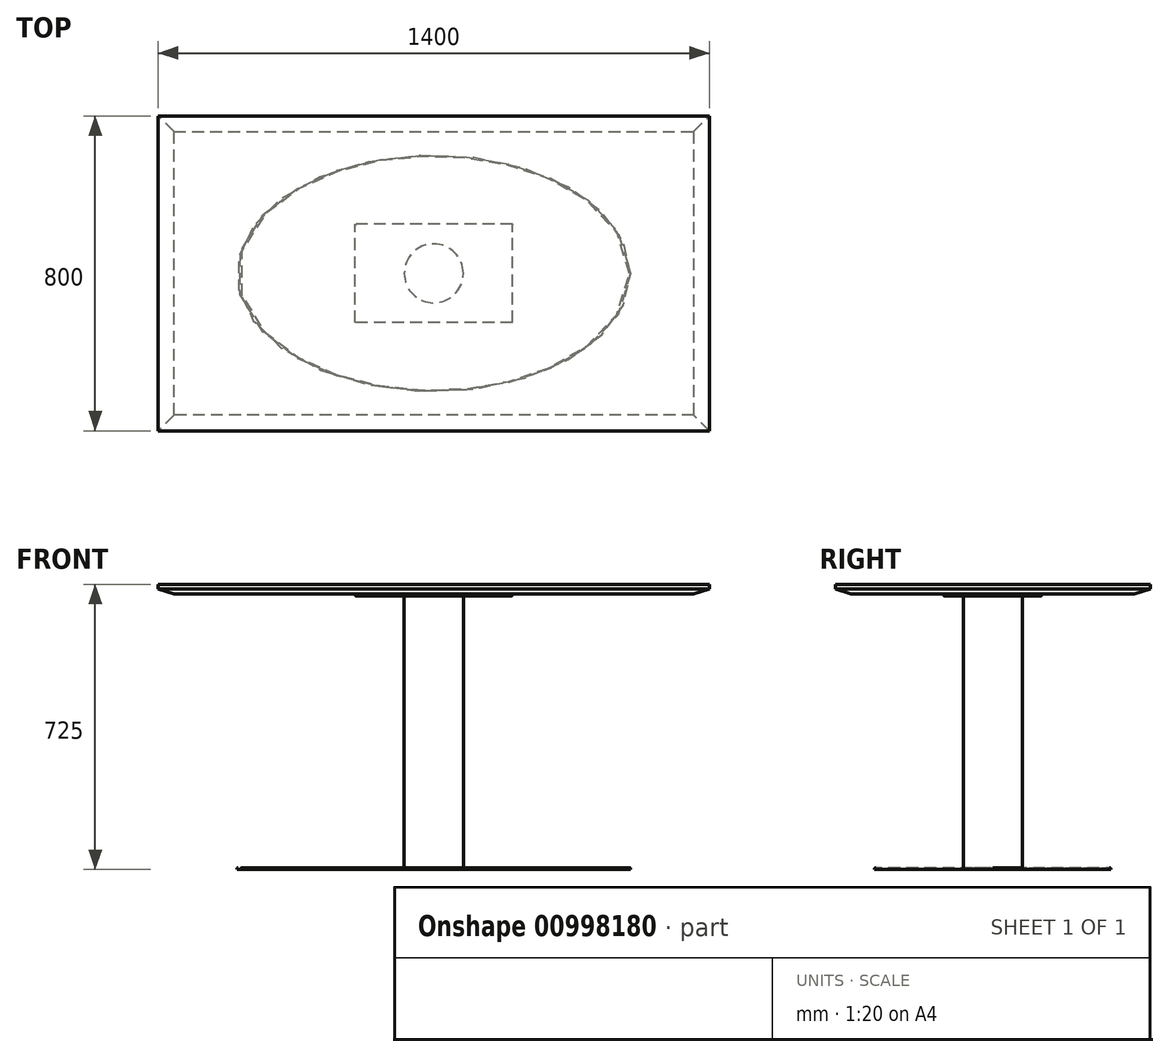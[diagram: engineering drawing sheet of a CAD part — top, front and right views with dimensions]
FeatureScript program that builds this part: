
annotation { "Feature Type Name" : "Feature", "Feature Type Description" : "" }
export const myFeature = defineFeature(function(context is Context, id is Id, definition is map)
    precondition{}
    {
        {
            var Q0;
            Q0=qCreatedBy(makeId("Top.planeOp"),FACE);
            var sketch = newSketch(context, id + "F0", { "sketchPlane" : qUnion([Q0])});
            skLineSegment(sketch, "E0.bottom", {"start": v(0, 0) * mm, "end": v(-1400, 0) * mm, "construction": true});
            skLineSegment(sketch, "E0.top", {"start": v(0, 800) * mm, "end": v(-1400, 800) * mm, "construction": true});
            skLineSegment(sketch, "E0.left", {"start": v(0, 0) * mm, "end": v(0, 800) * mm, "construction": true});
            skLineSegment(sketch, "E0.right", {"start": v(-1400, 0) * mm, "end": v(-1400, 800) * mm, "construction": true});
            skEllipse(sketch, "E1", {"center": v(-700, 400) * mm, "majorRadius": 500 * mm, "minorRadius": 300 * mm, "majorAxis": v(1, 0)});
            skPoint(sketch, "E1.centerSnap0", {"position": v(0, 400) * mm});
            skPoint(sketch, "E1.centerSnap1", {"position": v(-700, 0) * mm});
            skSolve(sketch);
        }
        {
            var Q0;
            Q0 = qSketchRegion(id + "F0", true);
            extrude(context, id + "F1", {"entities" : qUnion([Q0]), "depth" : 5 * mm, "offsetDistance" : 25 * mm});
        }
        {
            var Q0;
            Q0=makeQuery(id+"F1.opExtrude","CAP_FACE",FACE,{"disambiguationData":[OSD([sQuery(id+"F0.wireOp",EDGE,"E1")])],"isStart":false});
            fillet(context, id + "F2", {"entities" : qUnion([Q0]), "radius" : 3 * mm, "tangentPropagation" : true, "allowEdgeOverflow" : false});
        }
        {
            var Q0;
            Q0=makeQuery(id+"F1.opExtrude","CAP_FACE",FACE,{"disambiguationData":[OSD([sQuery(id+"F0.wireOp",EDGE,"E1")])],"isStart":false});
            cPlane(context, id + "F3", {"entities" : qUnion([Q0]), "cplaneType" : CPlaneType.OFFSET, "offset" : 0 * mm, "width" : 150 * mm, "height" : 150 * mm});
        }
        {
            var Q0;
            Q0=qCreatedBy(id+"F3.planeOp",FACE);
            var sketch = newSketch(context, id + "F4", { "sketchPlane" : qUnion([Q0])});
            skLineSegment(sketch, "E2", {"start": v(0, 0) * mm, "end": v(-700, 0) * mm, "construction": true});
            skLineSegment(sketch, "E3", {"start": v(-700, 0) * mm, "end": v(-700, 400) * mm, "construction": true});
            skCircle(sketch, "E4", {"center": v(-700, 400) * mm, "radius": 75 * mm});
            skSolve(sketch);
        }
        {
            var Q0;
            Q0 = qSketchRegion(id + "F4", true);
            extrude(context, id + "F5", {"entities" : qUnion([Q0]), "operationType" : NewBodyOperationType.ADD, "depth" : 690 * mm, "offsetDistance" : 25 * mm});
        }
        {
            var Q0;
            Q0=makeQuery(id+"F5.opExtrude","CAP_FACE",FACE,{"disambiguationData":[OSD([sQuery(id+"F4.wireOp",EDGE,"E4")])],"isStart":false});
            cPlane(context, id + "F6", {"entities" : qUnion([Q0]), "cplaneType" : CPlaneType.OFFSET, "offset" : 0 * mm, "width" : 150 * mm, "height" : 150 * mm});
        }
        {
            var Q0;
            Q0=qCreatedBy(id+"F6.planeOp",FACE);
            var sketch = newSketch(context, id + "F7", { "sketchPlane" : qUnion([Q0])});
            skLineSegment(sketch, "E5", {"start": v(0, 0) * mm, "end": v(-700, 0) * mm, "construction": true});
            skLineSegment(sketch, "E6", {"start": v(-700, 0) * mm, "end": v(-700, 400) * mm, "construction": true});
            skLineSegment(sketch, "E7.bottom", {"start": v(-500, 275) * mm, "end": v(-900, 275) * mm});
            skLineSegment(sketch, "E7.top", {"start": v(-500, 525) * mm, "end": v(-900, 525) * mm});
            skLineSegment(sketch, "E7.left", {"start": v(-500, 275) * mm, "end": v(-500, 525) * mm});
            skLineSegment(sketch, "E7.right", {"start": v(-900, 275) * mm, "end": v(-900, 525) * mm});
            skPoint(sketch, "E7.middle", {"position": v(-700, 400) * mm});
            skSolve(sketch);
        }
        {
            var Q0;
            Q0 = qSketchRegion(id + "F7", true);
            extrude(context, id + "F8", {"entities" : qUnion([Q0]), "operationType" : NewBodyOperationType.ADD, "depth" : 5 * mm, "offsetDistance" : 25 * mm});
        }
        {
            var Q0;
            Q0=makeQuery(id+"F8.opExtrude","CAP_EDGE",EDGE,{"disambiguationData":[OSD([sQuery(id+"F7.wireOp",EDGE,"E7.bottom")])],"isStart":true});
            var Q1;
            Q1=makeQuery(id+"F8.opExtrude","CAP_EDGE",EDGE,{"disambiguationData":[OSD([sQuery(id+"F7.wireOp",EDGE,"E7.right")])],"isStart":true});
            var Q2;
            Q2=makeQuery(id+"F8.opExtrude","CAP_EDGE",EDGE,{"disambiguationData":[OSD([sQuery(id+"F7.wireOp",EDGE,"E7.top")])],"isStart":true});
            var Q3;
            Q3=makeQuery(id+"F8.opExtrude","CAP_EDGE",EDGE,{"disambiguationData":[OSD([sQuery(id+"F7.wireOp",EDGE,"E7.left")])],"isStart":true});
            fillet(context, id + "F9", {"entities" : qUnion([Q0, Q1, Q2, Q3]), "radius" : 3 * mm, "tangentPropagation" : true, "allowEdgeOverflow" : false});
        }
        {
            var Q0;
            Q0=makeQuery(id+"F8.opExtrude","CAP_FACE",FACE,{"disambiguationData":[OSD([sQuery(id+"F7.wireOp",EDGE,"E7.bottom"),sQuery(id+"F7.wireOp",EDGE,"E7.top"),sQuery(id+"F7.wireOp",EDGE,"E7.left"),sQuery(id+"F7.wireOp",EDGE,"E7.right")])],"isStart":false});
            cPlane(context, id + "F10", {"entities" : qUnion([Q0]), "cplaneType" : CPlaneType.OFFSET, "offset" : 0 * mm, "width" : 150 * mm, "height" : 150 * mm});
        }
        {
            var Q0;
            Q0=qCreatedBy(id+"F10.planeOp",FACE);
            var sketch = newSketch(context, id + "F11", { "sketchPlane" : qUnion([Q0])});
            skLineSegment(sketch, "E8.bottom", {"start": v(0, 0) * mm, "end": v(-1400, 0) * mm});
            skLineSegment(sketch, "E8.top", {"start": v(0, 800) * mm, "end": v(-1400, 800) * mm});
            skLineSegment(sketch, "E8.left", {"start": v(0, 0) * mm, "end": v(0, 800) * mm});
            skLineSegment(sketch, "E8.right", {"start": v(-1400, 0) * mm, "end": v(-1400, 800) * mm});
            skSolve(sketch);
        }
        {
            var Q0;
            Q0 = qSketchRegion(id + "F11", true);
            extrude(context, id + "F12", {"entities" : qUnion([Q0]), "operationType" : NewBodyOperationType.ADD, "depth" : 25 * mm, "offsetDistance" : 25 * mm});
        }
        {
            var Q0;
            Q0=makeQuery(id+"F12.opExtrude","CAP_EDGE",EDGE,{"disambiguationData":[OSD([sQuery(id+"F11.wireOp",EDGE,"E8.right")])],"isStart":true});
            var Q1;
            Q1=makeQuery(id+"F12.opExtrude","CAP_EDGE",EDGE,{"disambiguationData":[OSD([sQuery(id+"F11.wireOp",EDGE,"E8.bottom")])],"isStart":true});
            var Q2;
            Q2=makeQuery(id+"F12.opExtrude","CAP_EDGE",EDGE,{"disambiguationData":[OSD([sQuery(id+"F11.wireOp",EDGE,"E8.left")])],"isStart":true});
            var Q3;
            Q3=makeQuery(id+"F12.opExtrude","CAP_EDGE",EDGE,{"disambiguationData":[OSD([sQuery(id+"F11.wireOp",EDGE,"E8.top")])],"isStart":true});
            chamfer(context, id + "F13", {"entities" : qUnion([Q0, Q1, Q2, Q3]), "chamferType" : ChamferType.TWO_OFFSETS, "width1" : 40 * mm, "oppositeDirection" : false, "width2" : 12.5 * mm, "tangentPropagation" : true});
        }
    });
